# Revit family: eeee
name_source: partatom
category: Lighting Fixtures
units: mm (PartAtom-declared; Revit-internal decimal feet)

## family parameters
Cut with Voids When Loaded = No
Host = Face
Light Source = Yes
OmniClass Number = 23.80.70.11
OmniClass Title = Luminaries for Internal Lighting
Part Type = Normal
Room Calculation Point = No
Round Connector Dimension = Use Diameter
Shared = No

## types (1)
- Not a type - Load Type Catalog!
    Apparent Load = 0 VA
    Assembly Code = D5020200
    CRI = 80
    Color Filter = 16777215
    Default Elevation = 4' - 0"
    Description = StarBar
    Dimming Lamp Color Temperature Shift = <None>
    Edition number = 1
    Emit Shape Visible in Rendering = No
    Frequency = 60 Hz
    Height = 0' - 1"
    Input Wattage = 0 W
    Keynote = 16500
    Lamp = LED
    Length = 4' - 0"
    Manufacturer = StarTek Lighting
    Model = StarBar
    Number of Poles = 3
    Phase = 1
    Photometric Note = Import IES files https://starteklightingamerica.com
    Photometric Web File = Generic Light Source Shown : Please download and link the IES file that best matches your fixture specification
    Power Factor = 0.93
    Product Guid = 2f96f888-5d7d-4f30-895e-11e65231a340
    Product data url = https://www.bimobject.com
    Type Comments = Linear Lighting Fixture
    URL = https://starteklightingamerica.com
    Voltage = 120 V
    Voltage Range = 120-277V
    Wattage Comments = Efficacy up to 150 lm/W
    Weight = 2.75 lbf
    Width = 0' - 2"
    z_AC = Aircraft Cable : with Canopy
    z_AL = Aircraft Cable : with Loops
    z_Lamp Length 4’ = Yes
    z_Lamp Length 8’ = No
    z_SM = Surface Mount : Surface Mount (SM)
    z_TM = T-Grid Mount : T-Grid Mount (TM)

## geometry (parser evidence)
native form markers: Sweep x10
no freeform markers — native parametric forms only
